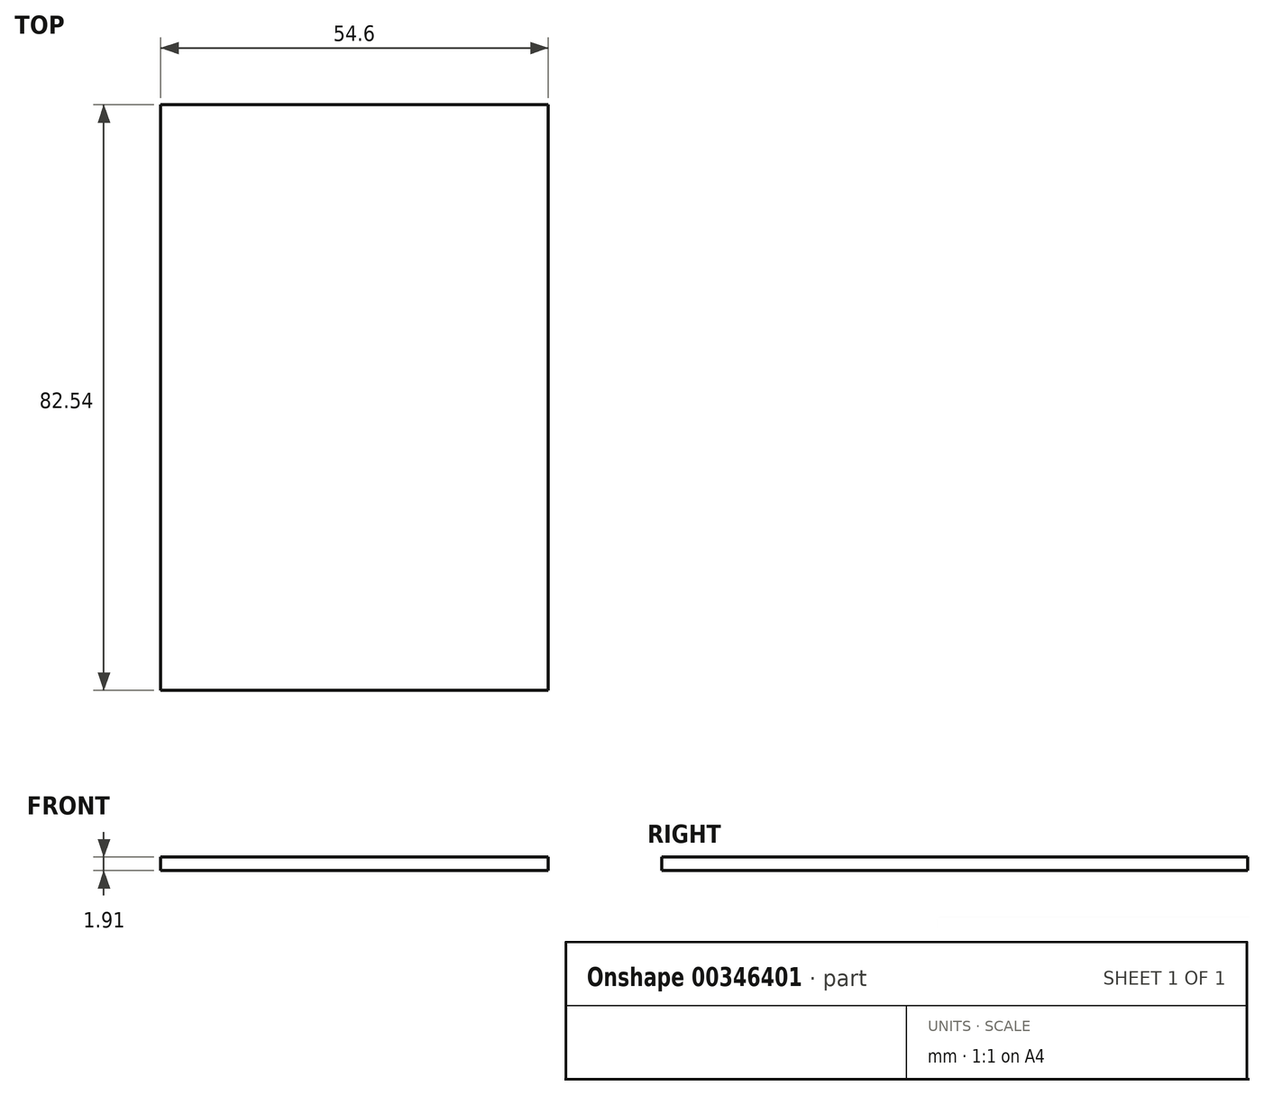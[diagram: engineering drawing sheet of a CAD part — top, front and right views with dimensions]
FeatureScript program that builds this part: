
annotation { "Feature Type Name" : "Feature", "Feature Type Description" : "" }
export const myFeature = defineFeature(function(context is Context, id is Id, definition is map)
    precondition{}
    {
        {
            var Q0;
            Q0=qCreatedBy(makeId("Top.planeOp"),FACE);
            var sketch = newSketch(context, id + "F0", { "sketchPlane" : qUnion([Q0])});
            skLineSegment(sketch, "E0.bottom", {"start": v(27.3, -41.28) * mm, "end": v(-27.3, -41.28) * mm});
            skLineSegment(sketch, "E0.top", {"start": v(27.3, 41.28) * mm, "end": v(-27.3, 41.28) * mm});
            skLineSegment(sketch, "E0.left", {"start": v(27.3, -41.27) * mm, "end": v(27.3, 41.28) * mm});
            skLineSegment(sketch, "E0.right", {"start": v(-27.3, -41.28) * mm, "end": v(-27.3, 41.27) * mm});
            skPoint(sketch, "E0.middle", {"position": v(0, 0) * mm});
            skSolve(sketch);
        }
        {
            var Q0;
            Q0=makeQuery(id+"F0.imprint","IMPRINT",FACE,{"disambiguationData":[TD([[makeQuery(id+"F0.imprint","IMPRINT",EDGE,{"derivedFrom":sQuery(id+"F0.wireOp",EDGE,"E0.bottom")}),-1.0]])]});
            extrude(context, id + "F1", {"entities" : qUnion([Q0]), "depth" : 1.9 * mm, "offsetDistance" : 25.4 * mm});
        }
    });
